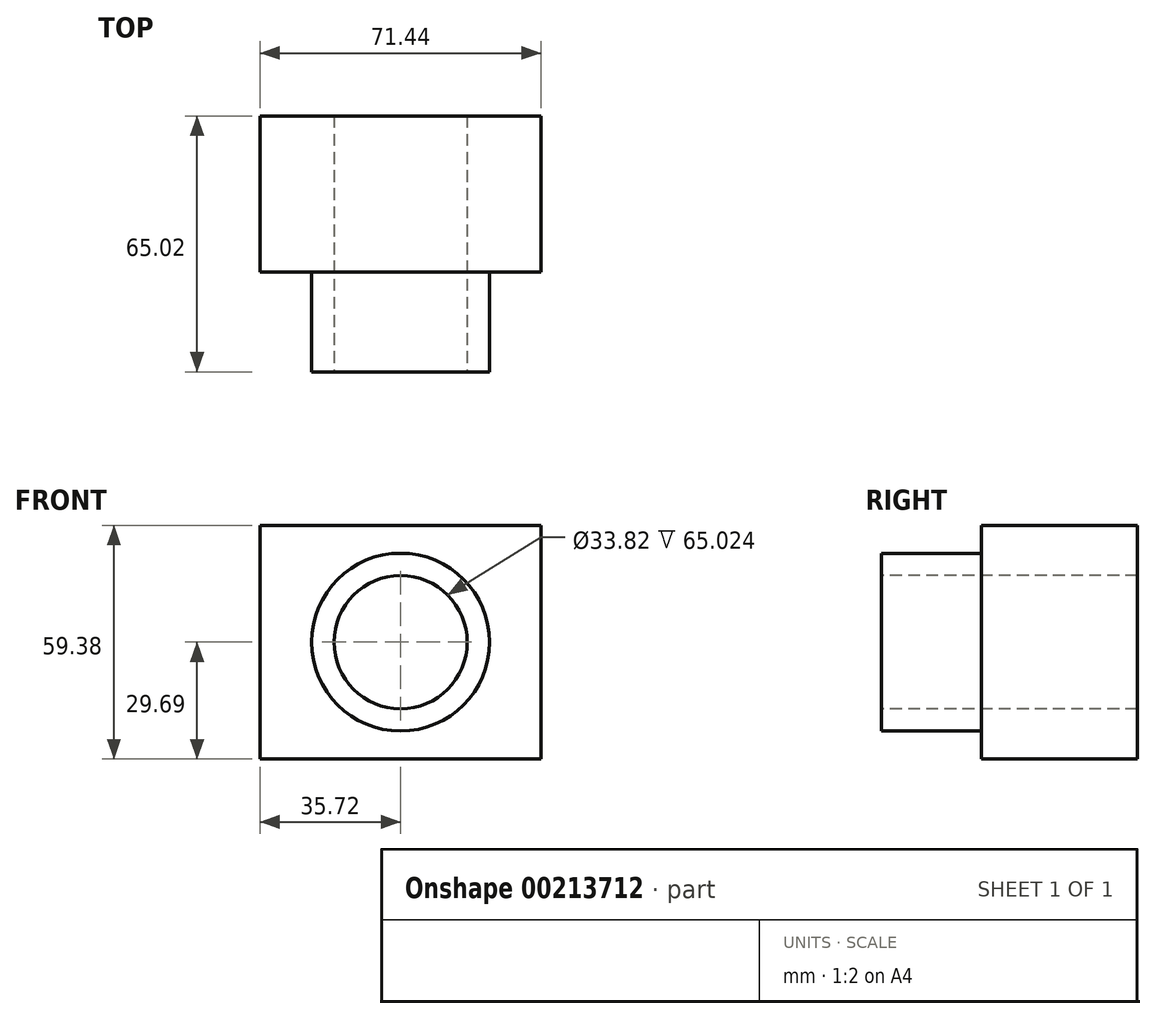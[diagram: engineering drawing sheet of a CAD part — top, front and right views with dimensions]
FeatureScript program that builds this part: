
annotation { "Feature Type Name" : "Feature", "Feature Type Description" : "" }
export const myFeature = defineFeature(function(context is Context, id is Id, definition is map)
    precondition{}
    {
        {
            var Q0;
            Q0=qCreatedBy(makeId("Front.planeOp"),FACE);
            var sketch = newSketch(context, id + "F0", { "sketchPlane" : qUnion([Q0])});
            skLineSegment(sketch, "E0.bottom", {"start": v(35.72, -29.7) * mm, "end": v(-35.72, -29.7) * mm});
            skLineSegment(sketch, "E0.top", {"start": v(35.72, 29.7) * mm, "end": v(-35.72, 29.7) * mm});
            skLineSegment(sketch, "E0.left", {"start": v(35.72, -29.7) * mm, "end": v(35.72, 29.7) * mm});
            skLineSegment(sketch, "E0.right", {"start": v(-35.72, -29.7) * mm, "end": v(-35.72, 29.7) * mm});
            skPoint(sketch, "E0.middle", {"position": v(0, 0) * mm});
            skSolve(sketch);
        }
        {
            var Q0;
            Q0 = qSketchRegion(id + "F0", true);
            extrude(context, id + "F1", {"entities" : qUnion([Q0]), "depth" : 39.62 * mm});
        }
        {
            var Q0;
            Q0=makeQuery(id+"F1.opExtrude","CAP_FACE",FACE,{"disambiguationData":[OSD([sQuery(id+"F0.wireOp",EDGE,"E0.bottom"),sQuery(id+"F0.wireOp",EDGE,"E0.top"),sQuery(id+"F0.wireOp",EDGE,"E0.left"),sQuery(id+"F0.wireOp",EDGE,"E0.right")])],"isStart":false});
            var sketch = newSketch(context, id + "F2", { "sketchPlane" : qUnion([Q0])});
            skCircle(sketch, "E1", {"center": v(0, 0) * mm, "radius": 22.6 * mm});
            skSolve(sketch);
        }
        {
            var Q0;
            Q0 = qSketchRegion(id + "F2", true);
            extrude(context, id + "F3", {"entities" : qUnion([Q0]), "operationType" : NewBodyOperationType.ADD, "depth" : 25.4 * mm});
        }
        {
            var Q0;
            Q0=makeQuery(id+"F3.opExtrude","CAP_FACE",FACE,{"disambiguationData":[OSD([sQuery(id+"F2.wireOp",EDGE,"E1")])],"isStart":false});
            var sketch = newSketch(context, id + "F4", { "sketchPlane" : qUnion([Q0])});
            skCircle(sketch, "E2", {"center": v(0, 0) * mm, "radius": 16.91 * mm});
            skSolve(sketch);
        }
        {
            var Q0;
            Q0 = qSketchRegion(id + "F4", true);
            extrude(context, id + "F5", {"entities" : qUnion([Q0]), "operationType" : NewBodyOperationType.REMOVE, "endBound" : BoundingType.THROUGH_ALL, "oppositeDirection" : true, "depth" : 25.4 * mm});
        }
    });
